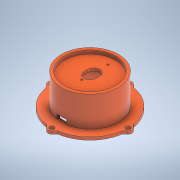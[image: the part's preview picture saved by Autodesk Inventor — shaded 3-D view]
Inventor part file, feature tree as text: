
AUTODESK INVENTOR PART (.ipt)
format: ipt  version: 2021 (Build 250183000, 183)  size: 293,888 bytes
history: native  units: mm
features: extrude x7, sketch x5, projected_geometry x5, other x1
ambient origin geometry x8: Origin, YZ Plane, XZ Plane, XY Plane, X Axis, Y Axis, Z Axis, Center Point
bodies: Body1 (feature_tree)
feature tree (18):
  other  "Sólido1"
  sketch  "Boceto1"  dims[d0=12.5mm d1=5.0mm]
  extrude  "Extrusión1"  Depth=5.0mm
  extrude  "Extrusión2"  Depth=6.0mm
  extrude  "Extrusión3"  Depth=2.5mm
  extrude  "Extrusión4"  Depth=5.0mm
  extrude  "Extrusión5"  Depth=12.5mm
  extrude  "Extrusión6"  Depth=12.5mm
  extrude  "Extrusión7"  Depth=40.0mm
  sketch  "Boceto2"  dims[d2=2.0mm d4=6.0mm]
  projected_geometry  "Contorno proyectado1"
  projected_geometry  "Contorno proyectado2"
  sketch  "Boceto3"  dims[d6=2.0mm d7=2.5mm]
  sketch  "Boceto4"  dims[d8=12.5mm d9=5.0mm]
  sketch  "Boceto5"  dims[d10=6.25mm d11=12.5mm d13=12.5mm d14=54.0mm d15=60.0mm d16=3.0mm d17=0.0mm d18=6.8mm d19=0.0mm d20=5.0mm d21=0.0mm d22=2.0mm d23=2.0mm d24=6.0mm d25=3.0mm d26=0.0mm d27=60.0mm d28=54.0mm d29=25.0mm d30=0.0mm d31=80.0mm d32=60.0mm d33=54.0mm d34=5.0mm d35=8.0mm d36=5.0mm d37=8.0mm d38=5.0mm d39=8.0mm d40=5.0mm d41=8.0mm d42=10.0mm d43=10.0mm d44=3.0mm d45=0.0mm d46=5.0mm d47=10.0mm d48=10.0mm d49=5.0mm d50=40.0mm d51=0.0mm]
  projected_geometry  "Contorno proyectado3"
  projected_geometry  "Contorno proyectado4"
  projected_geometry  "Contorno proyectado5"
